# Revit family: TY-B-TY4951_Imperial
name_source: partatom
category: Sprinklers
units: mm (PartAtom-declared; Revit-internal decimal feet)

## family parameters
Always vertical = Yes
Cut with Voids When Loaded = No
Maintain Annotation Orientation = No
OmniClass Number = 23.65.70.17.11.24
OmniClass Title = Fire Fighting Sprinkler Heads
Part Type = Normal
Room Calculation Point = No
Round Connector Dimension = Use Diameter
Shared = No
Work Plane-Based = No

## types (26) — shared parameters
COBie = Yes
COBie.Component.Name = Sprinklers:Pendent_SIN
COBie.Type = Yes
COBie.Type.AssetType = Fixed
COBie.Type.Category = Pr_70_55_97_84:Sprinklers
COBie.Type.DurationUnit = year
COBie.Type.Manufacturer = Tyco Fire Protection Products
COBie.Type.Material = Bronze
COBie.Type.NominalHeight = 0' - 0"
COBie.Type.NominalLength = 0' - 0"
COBie.Type.NominalWidth = 0' - 0"
COBie.Type.Shape = Cylinder
Coverage = Standard
Coverage_ = Standard
Default Elevation = 0' - 0"
K-Factor = 7.9771
Manufacturer = Tyco Fire Protection Products
Manufacturer URL = www.tyco-fire.com
Material_ = Bronze
Model = TY-B
Nominal Diameter 1 = 1"
Orifice = Extra Large
Orifice Size = 0"
Outside Diameter 1 = 1"
Response = Standard
Response_ = Standard
SIN No = TY4951
Takeout 1 = 2"
Technical Data Sheet  No = TFP151
zero-valued in all types: COBie.Type.ReplacementCost, Style Id

## per-type parameters (varying)
| type | COBie.Component.Description | COBie.Type.Colour | COBie.Type.Finish | COBie.Type.ModelNumber | COBie.Type.ModelReference | COBie.Type.Size | COBie.Type.WarrantyGuarantorParts | Description | Finish_ | Part No | Temperature Rating |
| Pendent ½" NPT 135°F Brass_57-561-1-135 | TY-B Wet Pendent  135°F K8.0 1/2 NPT Br | Yellow | Natural Brass | 57-561-1-135 | TY-B Wet Pendent  135°F K8.0 1/2 NPT Br | 1/2"(DN15) | http://tycofsbp.com
TFPPTerms_of_Sale.pdf | TY-B Pendent Brass 135°F 8K ½" NPT | Natural Brass | 57-561-1-135 | 135 °F |
| Pendent ½" NPT 155°F Brass_57-561-1-155 | TY-B Wet Pendent  155°F K8.0 1/2 NPT Br | Yellow | Natural Brass | 57-561-1-155 | TY-B Wet Pendent  155°F K8.0 1/2 NPT Br | 1/2"(DN15) | http://tycofsbp.com
TFPPTerms_of_Sale.pdf | TY-B Pendent Brass 155°F 8K ½" NPT | Natural Brass | 57-561-1-155 | 155 °F |
| Pendent ½" NPT 175°F Brass_57-561-1-175 | TY-B Wet Pendent  175°F K8.0 1/2 NPT Br | Yellow | Natural Brass | 57-561-1-175 | TY-B Wet Pendent  175°F K8.0 1/2 NPT Br | 1/2"(DN15) | http://tycofsbp.com
TFPPTerms_of_Sale.pdf | TY-B Pendent Brass 175°F 8K ½" NPT | Natural Brass | 57-561-1-175 | 175 °F |
| Pendent ½" NPT 200°F Brass_57-561-1-200 | TY-B Wet Pendent  200°F K8.0 1/2 NPT Br | Yellow | Natural Brass | 57-561-1-200 | TY-B Wet Pendent  200°F K8.0 1/2 NPT Br | 1/2"(DN15) | http://tycofsbp.com
TFPPTerms_of_Sale.pdf | TY-B Pendent Brass 200°F 8K ½" NPT | Natural Brass | 57-561-1-200 | 200 °F |
| Pendent ½" NPT 286°F Brass_57-561-1-286 | TY-B Wet Pendent  286°F K8.0 1/2 NPT Br | Yellow | Natural Brass | 57-561-1-286 | TY-B Wet Pendent  286°F K8.0 1/2 NPT Br | 1/2"(DN15) | http://tycofsbp.com
TFPPTerms_of_Sale.pdf | TY-B Pendent Brass 286°F 8K ½" NPT | Natural Brass | 57-561-1-286 | 286 °F |
| Pendent ½" NPT 360°F Brass_57-561-1-360 | TY-B Wet Pendent  360°F K8.0 1/2 NPT Br | Yellow | Natural Brass | 57-561-1-360 | TY-B Wet Pendent  360°F K8.0 1/2 NPT Br | 1/2"(DN15) | http://tycofsbp.com
TFPPTerms_of_Sale.pdf | TY-B Pendent Brass 360°F 8K ½" NPT | Natural Brass | 57-561-1-360 | 360 °F |
| Pendent ½" NPT 135°F White_57-561-3-135 | TY-B Wet Pendent  135°F K8.0 1/2 NPT Wh9010 | White | Pure White | 57-561-3-135 | TY-B Wet Pendent  135°F K8.0 1/2 NPT Wh9010 | 1/2"(DN20) | http://tycofsbp.com
TFPPTerms_of_Sale.pdf | TY-B Pendent White 135°F 8K ½" NPT | White RAL9010 | 57-561-3-135 | 135 °F |
| Pendent ½" NPT 155°F White_57-561-3-155 | TY-B Wet Pendent  155°F K8.0 1/2 NPT Wh9010 | White | Pure White | 57-561-3-155 | TY-B Wet Pendent  155°F K8.0 1/2 NPT Wh9010 | 1/2"(DN15) | http://tycofsbp.com
TFPPTerms_of_Sale.pdf | TY-B Pendent White 155°F 8K ½" NPT | White RAL9010 | 57-561-3-155 | 155 °F |
| Pendent ½" NPT 175°F White_57-561-3-175 | TY-B Wet Pendent  175°F K8.0 1/2 NPT Wh9010 | White | Pure White | 57-561-3-175 | TY-B Wet Pendent  175°F K8.0 1/2 NPT Wh9010 | 1/2"(DN15) | http://tycofsbp.com
TFPPTerms_of_Sale.pdf | TY-B Pendent White 175°F 8K ½" NPT | White RAL9010 | 57-561-3-175 | 175 °F |
| Pendent ½" NPT 200°F White_57-561-3-200 | TY-B Wet Pendent  200°F K8.0 1/2 NPT Wh9010 | White | Pure White | 57-561-3-200 | TY-B Wet Pendent  200°F K8.0 1/2 NPT Wh9010 | 1/2"(DN15) | http://tycofsbp.com
TFPPTerms_of_Sale.pdf | TY-B Pendent White 200°F 8K ½" NPT | White RAL9010 | 57-561-3-200 | 200 °F |
| Pendent ½" NPT 286°F White_57-561-3-286 | TY-B Wet Pendent  286°F K8.0 1/2 NPT Wh9010 | White | Pure White | 57-561-3-286 | TY-B Wet Pendent  286°F K8.0 1/2 NPT Wh9010 | 1/2"(DN15) | http://tycofsbp.com
TFPPTerms_of_Sale.pdf | TY-B Pendent White 286°F 8K ½" NPT | White RAL9010 | 57-561-3-286 | 286 °F |
| Pendent ½" NPT 360°F White_57-561-3-360 | TY-B Wet Pendent  360°F K8.0 1/2 NPT Wh9010 | White | Pure White | 57-561-3-360 | TY-B Wet Pendent  360°F K8.0 1/2 NPT Wh9010 | 1/2"(DN15) | http://tycofsbp.com
TFPPTerms_of_Sale.pdf | TY-B Pendent White 360°F 8K ½" NPT | White RAL9010 | 57-561-3-360 | 360 °F |
| Pendent ½" NPT 135°F White_57-561-4-135 | TY-B Wet Pendent  135°F K8.0 1/2 NPT Wh9003 | White | Signal White | 57-561-4-135 | TY-B Wet Pendent  135°F K8.0 1/2 NPT Wh9003 | 1/2"(DN15) | http://tycofsbp.com | TY-B Pendent White 135°F 8K ½" NPT | White RAL9003 | 57-561-4-135 | 135 °F |
| Pendent ½" NPT 155°F White_57-561-4-155 | TY-B Wet Pendent  155°F K8.0 1/2 NPT Wh9003 | White | Signal White | 57-561-4-155 | TY-B Wet Pendent  155°F K8.0 1/2 NPT Wh9003 | 1/2"(DN15) | http://tycofsbp.com | TY-B Pendent White 155°F 8K ½" NPT | White RAL9003 | 57-561-4-155 | 155 °F |
| Pendent ½" NPT 175°F White_57-561-4-175 | TY-B Wet Pendent  175°F K8.0 1/2 NPT Wh9003 | White | Signal White | 57-561-4-175 | TY-B Wet Pendent  175°F K8.0 1/2 NPT Wh9003 | 1/2"(DN15) | http://tycofsbp.com | TY-B Pendent White 175°F 8K ½" NPT | White RAL9003 | 57-561-4-175 | 175 °F |
| Pendent ½" NPT 200°F White_57-561-4-200 | TY-B Wet Pendent  200°F K8.0 1/2 NPT Wh9003 | White | Signal White | 57-561-4-200 | TY-B Wet Pendent  200°F K8.0 1/2 NPT Wh9003 | 1/2"(DN15) | http://tycofsbp.com | TY-B Pendent White 200°F 8K ½" NPT | White RAL9003 | 57-561-4-200 | 200 °F |
| Pendent ½" NPT 286°F White_57-561-4-286 | TY-B Wet Pendent  286°F K8.0 1/2 NPT Wh9003 | White | Signal White | 57-561-4-286 | TY-B Wet Pendent  286°F K8.0 1/2 NPT Wh9003 | 1/2"(DN15) | http://tycofsbp.com | TY-B Pendent White 286°F 8K ½" NPT | White RAL9003 | 57-561-4-286 | 286 °F |
| Pendent ½" NPT 360°F White_57-561-4-360 | TY-B Wet Pendent  360°F K8.0 1/2 NPT Wh9003 | White | Signal White | 57-561-4-360 | TY-B Wet Pendent  360°F K8.0 1/2 NPT Wh9003 | 1/2"(DN15) | http://tycofsbp.com | TY-B Pendent White 360°F 8K ½" NPT | White RAL9003 | 57-561-4-360 | 360 °F |
| Pendent ½" NPT 155°F JetBlack_57-561-5-155 | TY-B Wet Pendent  155°F K8.0 1/2 NPT JBlk | Black | Jet Black | 57-561-5-155 | TY-B Wet Pendent  155°F K8.0 1/2 NPT JBlk | 1/2"(DN15) | http://tycofsbp.com | TY-B Pendent JetBlack 155°F 8K ½" NPT | Jet Black RAL9005 | 57-561-5-155 | 155 °F |
| Pendent ½" NPT 155°F JetBlack_57-561-5-200 | TY-B Wet Pendent_Black_155   155°F K8.0 1/2 NPT JBlk | Black | Jet Black | 57-561-5-155 | TY-B Wet Pendent_Black_155   155°F K8.0 1/2 NPT JBlk | 1/2"(DN15) | http://tycofsbp.com | TY-B Pendent JetBlack 155°F 8K ½" NPT | JetBlack RAL9005 | 57-561-5-200 | 155 °F |
| Pendent ½" NPT 135°F Chrome_57-561-9-135 | TY-B Wet Pendent  135°F K8.0 1/2 NPT Chr | Silver | Chrome Plated | 57-561-9-135 | TY-B Wet Pendent  135°F K8.0 1/2 NPT Chr | 1/2"(DN15) | http://tycofsbp.com
TFPPTerms_of_Sale.pdf | TY-B Pendent Chrome 135°F 8K ½" NPT | Chrome Plated | 57-561-9-135 | 135 °F |
| Pendent ½" NPT 155°F Chrome_57-561-9-155 | TY-B Wet Pendent  155°F K8.0 1/2 NPT Chr | Silver | Chrome Plated | 57-561-9-155 | TY-B Wet Pendent  155°F K8.0 1/2 NPT Chr | 1/2"(DN15) | http://tycofsbp.com
TFPPTerms_of_Sale.pdf | TY-B Pendent Chrome 155°F 8K ½" NPT | Chrome Plated | 57-561-9-155 | 155 °F |
| Pendent ½" NPT 175°F Chrome_57-561-9-175 | TY-B Wet Pendent  175°F K8.0 1/2 NPT Chr | Silver | Chrome Plated | 57-561-9-175 | TY-B Wet Pendent  175°F K8.0 1/2 NPT Chr | 1/2"(DN15) | http://tycofsbp.com
TFPPTerms_of_Sale.pdf | TY-B Pendent Chrome 175°F 8K ½" NPT | Chrome Plated | 57-561-9-175 | 175 °F |
| Pendent ½" NPT 200°F Chrome_57-561-9-200 | TY-B Wet Pendent  200°F K8.0 1/2 NPT Chr | Silver | Chrome PLated | 57-561-9-200 | TY-B Wet Pendent  200°F K8.0 1/2 NPT Chr | 1/2"(DN15) | http://tycofsbp.com
TFPPTerms_of_Sale.pdf | TY-B Pendent Chrome 200°F 8K ½" NPT | Chrome Plated | 57-561-9-200 | 200 °F |
| Pendent ½" NPT 286°F Chrome_57-561-9-286 | TY-B Wet Pendent  286°F K8.0 1/2 NPT Chr | Silver | Chrome Plated | 57-561-9-286 | TY-B Wet Pendent  286°F K8.0 1/2 NPT Chr | 1/2"(DN15) | http://tycofsbp.com
TFPPTerms_of_Sale.pdf | TY-B Pendent Chrome 286°F 8K ½" NPT | Chrome Plated | 57-561-9-286 | 286 °F |
| Pendent ½" NPT 360°F Chrome_57-561-9-360 | TY-B Wet Pendent  360°F K8.0 1/2 NPT Chr | Silver | Chrome Plated | 57-561-9-360 | TY-B Wet Pendent  360°F K8.0 1/2 NPT Chr | 1/2"(DN15) | http://tycofsbp.com
TFPPTerms_of_Sale.pdf | TY-B Pendent Chrome 360°F 8K ½" NPT | Chrome Plated | 57-561-9-360 | 360 °F |

## geometry (parser evidence)
native form markers: Blend x2, Sweep x53
no freeform markers — native parametric forms only
